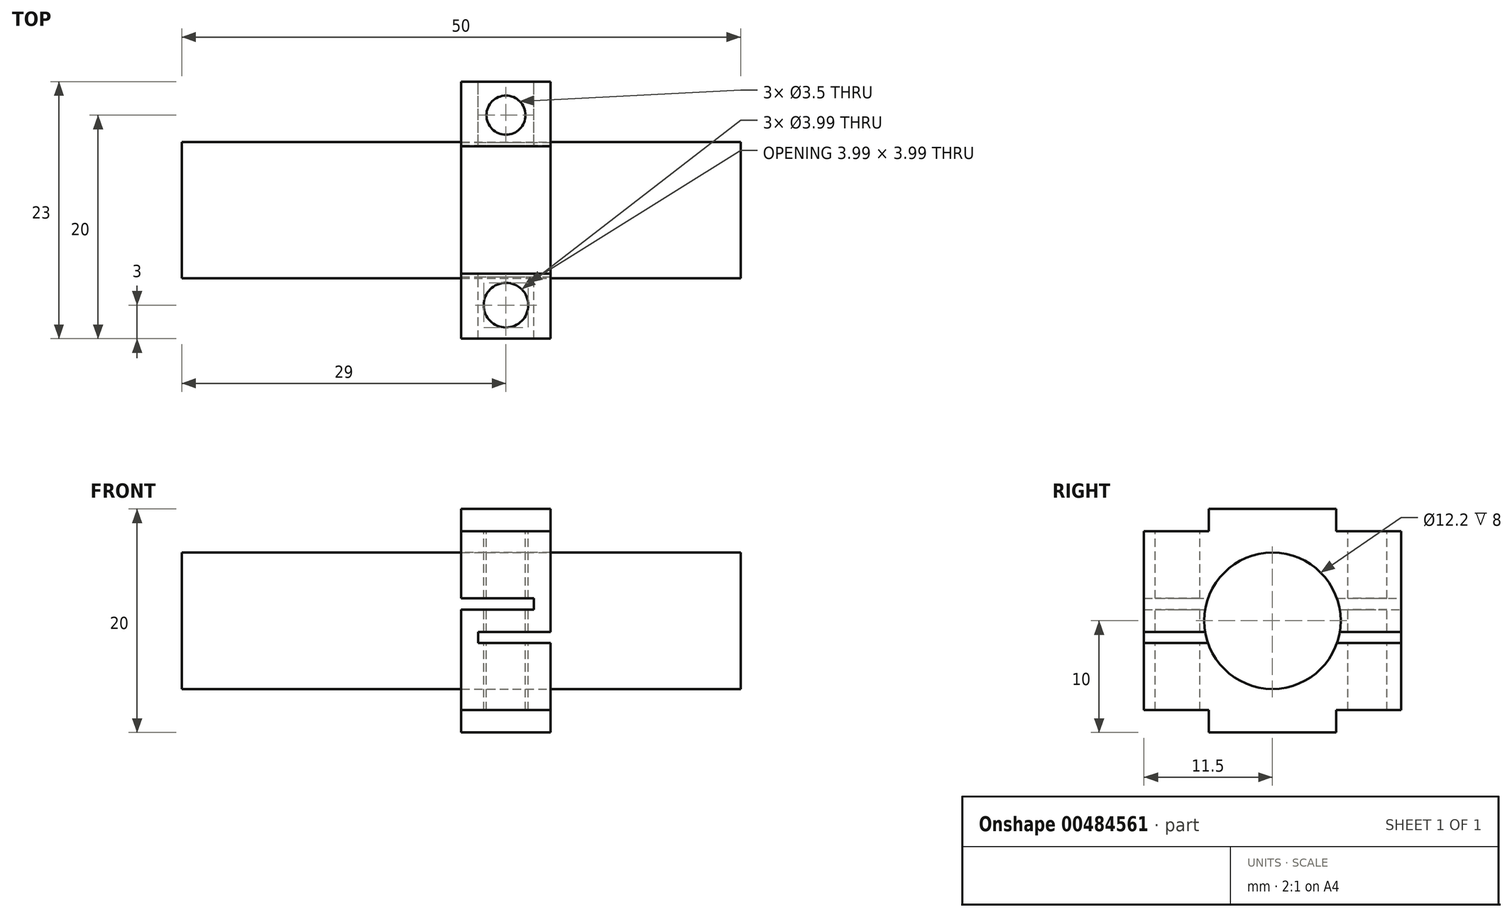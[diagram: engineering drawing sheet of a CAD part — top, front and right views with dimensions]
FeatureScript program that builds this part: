
annotation { "Feature Type Name" : "Feature", "Feature Type Description" : "" }
export const myFeature = defineFeature(function(context is Context, id is Id, definition is map)
    precondition{}
    {
        {
            var Q0;
            Q0=qCreatedBy(makeId("Front.planeOp"),FACE);
            var sketch = newSketch(context, id + "F0", { "sketchPlane" : qUnion([Q0])});
            skLineSegment(sketch, "E0", {"start": v(-4, 10) * mm, "end": v(4, 10) * mm});
            skLineSegment(sketch, "E1", {"start": v(4, 10) * mm, "end": v(4, -1) * mm});
            skLineSegment(sketch, "E2", {"start": v(4, -10) * mm, "end": v(-4, -10) * mm});
            skLineSegment(sketch, "E3", {"start": v(-4, -10) * mm, "end": v(-4, 1) * mm});
            skLineSegment(sketch, "E4", {"start": v(-4, 2) * mm, "end": v(2.5, 2) * mm});
            skLineSegment(sketch, "E5", {"start": v(2.5, 2) * mm, "end": v(2.5, 1) * mm});
            skLineSegment(sketch, "E6", {"start": v(2.5, 1) * mm, "end": v(-4, 1) * mm});
            skLineSegment(sketch, "E7", {"start": v(4, -1) * mm, "end": v(-2.5, -1) * mm});
            skLineSegment(sketch, "E8", {"start": v(-2.5, -1) * mm, "end": v(-2.5, -2) * mm});
            skLineSegment(sketch, "E9", {"start": v(-2.5, -2) * mm, "end": v(4, -2) * mm});
            skLineSegment(sketch, "E10.trimOffspring", {"start": v(-4, 2) * mm, "end": v(-4, 10) * mm});
            skLineSegment(sketch, "E11.trimOffspring", {"start": v(4, -2) * mm, "end": v(4, -10) * mm});
            skSolve(sketch);
        }
        {
            var Q0;
            Q0 = qSketchRegion(id + "F0", true);
            extrude(context, id + "F1", {"entities" : qUnion([Q0]), "endBound" : BoundingType.SYMMETRIC, "depth" : 23 * mm});
        }
        {
            var Q0;
            Q0=qCreatedBy(makeId("Top.planeOp"),FACE);
            var sketch = newSketch(context, id + "F2", { "sketchPlane" : qUnion([Q0])});
            skCircle(sketch, "E12", {"center": v(0, 8.5) * mm, "radius": 1.75 * mm});
            skCircle(sketch, "E13", {"center": v(0, -8.5) * mm, "radius": 2 * mm});
            skSolve(sketch);
        }
        {
            var Q0;
            Q0 = qSketchRegion(id + "F2", true);
            extrude(context, id + "F3", {"entities" : qUnion([Q0]), "operationType" : NewBodyOperationType.REMOVE, "endBound" : BoundingType.SYMMETRIC, "oppositeDirection" : true, "depth" : 40 * mm});
        }
        {
            var Q0;
            Q0=qCreatedBy(makeId("Right.planeOp"),FACE);
            var sketch = newSketch(context, id + "F4", { "sketchPlane" : qUnion([Q0])});
            skCircle(sketch, "E14", {"center": v(0, 0) * mm, "radius": 6.1 * mm});
            skSolve(sketch);
        }
        {
            var Q0;
            Q0 = qSketchRegion(id + "F4", true);
            extrude(context, id + "F5", {"entities" : qUnion([Q0]), "operationType" : NewBodyOperationType.REMOVE, "endBound" : BoundingType.SYMMETRIC, "depth" : 25 * mm});
        }
        {
            var Q0;
            Q0=qCreatedBy(makeId("Right.planeOp"),FACE);
            var sketch = newSketch(context, id + "F6", { "sketchPlane" : qUnion([Q0])});
            skLineSegment(sketch, "E15.bottom", {"start": v(-5.7, 10) * mm, "end": v(-11.5, 10) * mm});
            skLineSegment(sketch, "E15.top", {"start": v(-5.7, 8) * mm, "end": v(-11.5, 8) * mm});
            skLineSegment(sketch, "E15.left", {"start": v(-5.7, 10) * mm, "end": v(-5.7, 8) * mm});
            skLineSegment(sketch, "E15.right", {"start": v(-11.5, 10) * mm, "end": v(-11.5, 8) * mm});
            skLineSegment(sketch, "E16.MirrorCS", {"start": v(5.7, 10) * mm, "end": v(5.7, 8) * mm});
            skLineSegment(sketch, "E17.MirrorCS", {"start": v(5.7, 8) * mm, "end": v(11.5, 8) * mm});
            skLineSegment(sketch, "E18.MirrorCS", {"start": v(11.5, 10) * mm, "end": v(11.5, 8) * mm});
            skLineSegment(sketch, "E19.MirrorCS", {"start": v(5.7, 10) * mm, "end": v(11.5, 10) * mm});
            skLineSegment(sketch, "E20.MirrorCS", {"start": v(5.7, -8) * mm, "end": v(11.5, -8) * mm});
            skLineSegment(sketch, "E21.MirrorCS", {"start": v(5.7, -10) * mm, "end": v(5.7, -8) * mm});
            skLineSegment(sketch, "E22.MirrorCS", {"start": v(5.7, -10) * mm, "end": v(11.5, -10) * mm});
            skLineSegment(sketch, "E23.MirrorCS", {"start": v(11.5, -10) * mm, "end": v(11.5, -8) * mm});
            skLineSegment(sketch, "E24.MirrorCS", {"start": v(-5.7, -10) * mm, "end": v(-5.7, -8) * mm});
            skLineSegment(sketch, "E25.MirrorCS", {"start": v(-5.7, -8) * mm, "end": v(-11.5, -8) * mm});
            skLineSegment(sketch, "E26.MirrorCS", {"start": v(-11.5, -10) * mm, "end": v(-11.5, -8) * mm});
            skLineSegment(sketch, "E27.MirrorCS", {"start": v(-5.7, -10) * mm, "end": v(-11.5, -10) * mm});
            skSolve(sketch);
        }
        {
            var Q0;
            Q0 = qSketchRegion(id + "F6", true);
            extrude(context, id + "F7", {"entities" : qUnion([Q0]), "operationType" : NewBodyOperationType.REMOVE, "endBound" : BoundingType.SYMMETRIC, "depth" : 25 * mm});
        }
        {
            var Q0;
            Q0=makeQuery(id+"F1.opExtrude","SWEPT_FACE",FACE,{"disambiguationData":[OSD([sQuery(id+"F0.wireOp",EDGE,"E10.trimOffspring")])]});
            var sketch = newSketch(context, id + "F8", { "sketchPlane" : qUnion([Q0])});
            skCircle(sketch, "E28", {"center": v(0, 0) * mm, "radius": 6.1 * mm});
            skSolve(sketch);
        }
        {
            var Q0;
            Q0 = qSketchRegion(id + "F8", true);
            extrude(context, id + "F9", {"entities" : qUnion([Q0]), "depth" : 25 * mm, "hasSecondDirection" : true, "secondDirectionOppositeDirection" : true, "secondDirectionDepth" : 25 * mm});
        }
    });
